# Revit family: NAU_Naughtone_Stng_Pullman2SEAT12
name_source: partatom
category: Furniture
revit_build: Autodesk Revit 2017 (Build: 20190508_0315(x64)
units: mm (PartAtom-declared; Revit-internal decimal feet)

## family parameters
Always vertical = Yes
Cut with Voids When Loaded = No
OmniClass Number = 23.40.20.00
OmniClass Title = General Furniture and Specialties
Room Calculation Point = No
Shared = Yes
Work Plane-Based = No

## types (4) — shared parameters
Assembly Code = E2020200
AssetType = Movable
BoothMaterial = NAU_Maharam_Fabric_Teatro_007Yellow
Category = Pr_40_50_12 : Chairs, seats and benches
Color = Various
CushionOffset = 10 mm  [stored 0.0328084 ft]
DurationUnit = year
FrameMaterial = NAU_Naughtone_EPC_White
IfcExportAs = IfcFurnishingElementType
IfcExportType = SOFA
IsBackBoard = Yes
Keynote = Pr_40_50_12
LegMaterial = NAU_Naughtone_Metal_Steel_White
MainColor = Various
ManufacturerAddress = Knaresborough Tech Park, Manse Lane, Knaresborough, HG5 8LF
ManufacturerName = Naughtone
ManufacturerURL = www.naughtone.com
NBSDescription = Seating
NBSReference = 45-35-72/352
NominalHeight = 1300 mm  [stored 4.26509 ft]
NominalLength = 1300 mm  [stored 4.26509 ft]
NominalWidth = 676 mm  [stored 2.21785 ft]
ProductInformation = www.naughtone.com/products/pullman/
SeatMaterial = NAU_Maharam_Fabric_Teatro_007Yellow
Shape = Rectangular
Size = 1300 x 675 x 1300mm
SustainabilityPerformance = FSC certifeied, SCS indoor advantage gold
TableMaterial = NAU_Naughtone_MFMDF_White
TableOffset = 200 mm  [stored 0.656168 ft]
TabletMaterial = NAU_Naughtone_Wood_Oak
URL = www.naughtone.com
Uniclass2015Code = Pr_40_50_12
Uniclass2015Title = Chairs, seats and benches
Uniclass2015Version = Products v1.15
Version = 1
WarrantyDescription = Request warranty information from naughtone
WarrantyDurationLabor = 7
WarrantyDurationParts = 7
WarrantyDurationUnit = year
zero-valued in all types: NumberOfChairs, WorksurfaceArea

## per-type parameters (varying)
| type | BIMObjectName | Description | Finish | IsLeftTablet | IsRightTablet | Material | Model | ModelNumber | ModelReference | Name |
| Pullman 2 seat sofa with 2 tablet arms PUL2HT2 | NAU_Naughtone_Seating_Pullman_2seatsofawith2tabletarms | Pullman 2 seat sofa with 2 tablet arms | Fabric upholstery, oak/walnut wooden legs or black/white steel legs, wooden table top with oak/walnut veneer, white/black laminate, or lino top | Yes | Yes | Fabric, plywood frame, foam, steel/wooden legs, wooden table top | PUL2HT2 | PUL2HT2 | Pullman 2 seat sofa with 2 tablet arms | Seating_Pullman_2seatsofawith2tabletarms_Naughtone |
| Pullman 2 seat sofa with tablet arm (right) PUL2HTR | NAU_Naughtone_Seating_Pullman_Pullman2seatsofawithtabletarmright | Pullman 2 seat sofa with tablet arm right | Fabric upholstery; white EPC/black EPC/oak/walnut legs; whiteEPC/black EPC tablet arm; white MFMDF/black MFMDF/oak veneer MDF/walnut veneerMDF tablet top | No | Yes | Fabric, plywood frame, foam, steel/wooden legs, wooden table top | PUL2HTR | PUL2HTR | Pullman 2 seat sofa with tablet arm right | Seating_Pullman_2seatsofawithtabletarmright_Naughtone |
| Pullman 2 seat sofa PUL2H | NAU_Naughtone_Seating_Pullman_2seatsofa | Pullman 2 seat sofa | Fabric upholstery; white EPC/black EPC/oak/walnut legs | No | No | Fabric, plywood frame, foam, steel or wood legs | PUL2H | PUL2H | Pullman 2 seat sofa | Seating_Pullman_2seatsofa_Naughtone |
| Pullman 2 seat sofa with tablet arm (left) PUL2HTL | NAU_Naughtone_Seating_Pullman_2seatsofawithtabletarmleft | Pullman 2 seat sofa with tablet arm left | Fabric upholstery; white EPC/black EPC/oak/walnut legs; whiteEPC/black EPC tablet arm; white MFMDF/black MFMDF/oak veneer MDF/walnut veneerMDF tablet top | Yes | No | Fabric, plywood frame, foam, steel/wooden legs, wooden table top | PUL2HTL | PUL2HTL | Pullman 2 seat sofa with tablet arm left | Seating_Pullman_2seatsofawithtabletarmleft_Naughtone |

note: [stored X ft] marks values corroborated as IEEE doubles in the binary element streams (Revit-internal decimal feet)

## geometry (parser evidence)
native form markers: Sweep x8
no freeform markers — native parametric forms only
